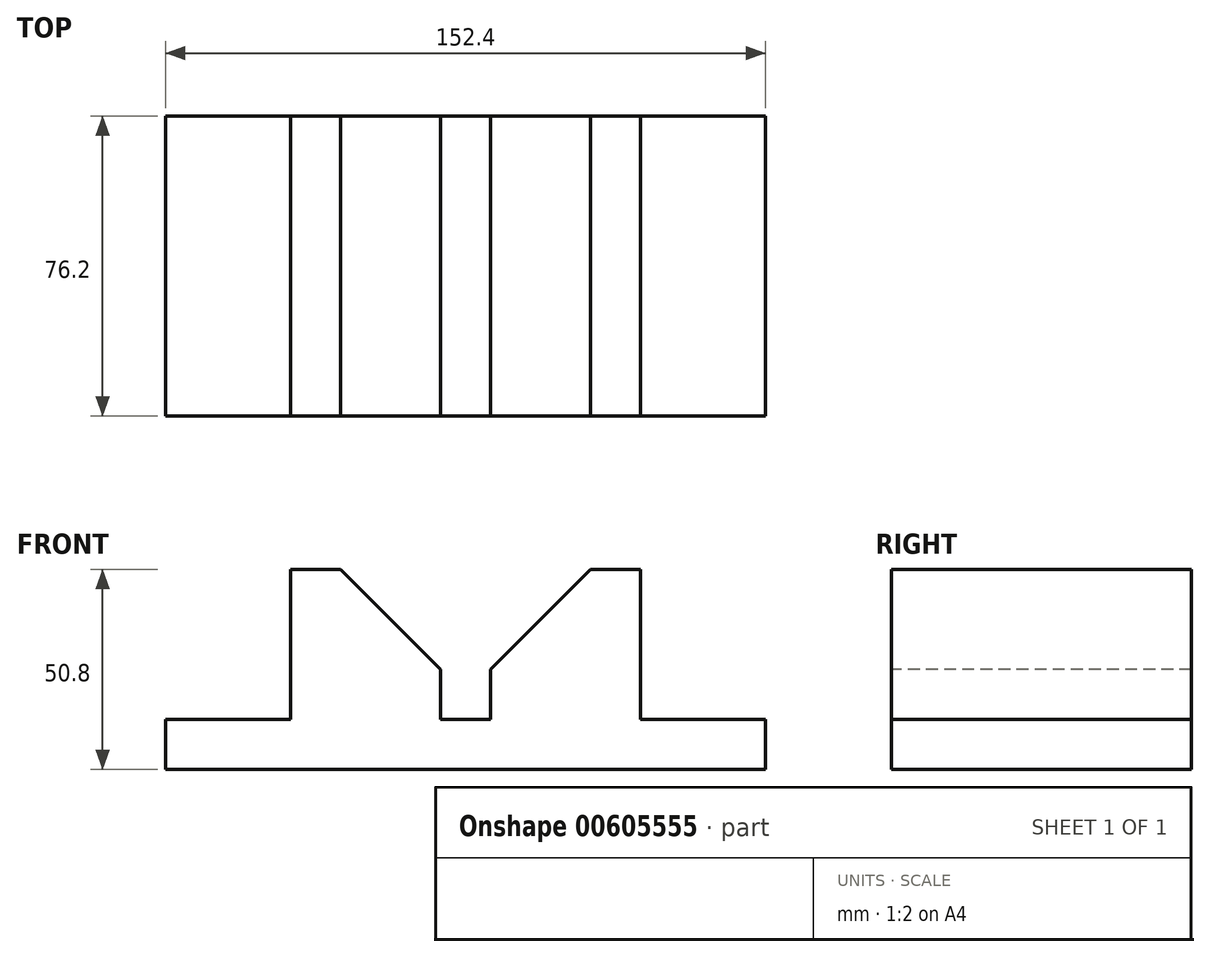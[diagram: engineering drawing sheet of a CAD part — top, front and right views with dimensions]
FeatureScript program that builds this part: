
annotation { "Feature Type Name" : "Feature", "Feature Type Description" : "" }
export const myFeature = defineFeature(function(context is Context, id is Id, definition is map)
    precondition{}
    {
        {
            var Q0;
            Q0=qCreatedBy(makeId("Front.planeOp"),FACE);
            var sketch = newSketch(context, id + "F0", { "sketchPlane" : qUnion([Q0])});
            skLineSegment(sketch, "E0", {"start": v(0, 0) * mm, "end": v(152.4, 0) * mm});
            skLineSegment(sketch, "E1", {"start": v(152.4, 0) * mm, "end": v(152.4, 12.7) * mm});
            skLineSegment(sketch, "E2", {"start": v(152.4, 12.7) * mm, "end": v(120.65, 12.7) * mm});
            skLineSegment(sketch, "E3", {"start": v(120.65, 12.7) * mm, "end": v(120.65, 50.8) * mm});
            skLineSegment(sketch, "E4", {"start": v(120.65, 50.8) * mm, "end": v(107.95, 50.8) * mm});
            skLineSegment(sketch, "E5", {"start": v(107.95, 50.8) * mm, "end": v(82.55, 25.4) * mm});
            skLineSegment(sketch, "E6", {"start": v(82.55, 25.4) * mm, "end": v(82.55, 12.7) * mm});
            skLineSegment(sketch, "E7", {"start": v(82.55, 12.7) * mm, "end": v(69.85, 12.7) * mm});
            skLineSegment(sketch, "E8", {"start": v(69.85, 12.7) * mm, "end": v(69.85, 25.4) * mm});
            skLineSegment(sketch, "E9", {"start": v(69.85, 25.4) * mm, "end": v(44.45, 50.8) * mm});
            skLineSegment(sketch, "E10", {"start": v(44.45, 50.8) * mm, "end": v(31.75, 50.8) * mm});
            skLineSegment(sketch, "E11", {"start": v(31.75, 50.8) * mm, "end": v(31.75, 12.7) * mm});
            skLineSegment(sketch, "E12", {"start": v(31.75, 12.7) * mm, "end": v(0, 12.7) * mm});
            skLineSegment(sketch, "E13", {"start": v(0, 12.7) * mm, "end": v(0, 0) * mm});
            skSolve(sketch);
        }
        {
            var Q0;
            Q0=makeQuery(id+"F0.imprint","IMPRINT",FACE,{"disambiguationData":[TD([[makeQuery(id+"F0.imprint","IMPRINT",EDGE,{"derivedFrom":sQuery(id+"F0.wireOp",EDGE,"E0")}),1.0]])]});
            extrude(context, id + "F1", {"entities" : qUnion([Q0]), "oppositeDirection" : true, "depth" : 76.2 * mm, "offsetDistance" : 25.4 * mm});
        }
    });
